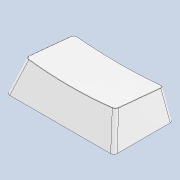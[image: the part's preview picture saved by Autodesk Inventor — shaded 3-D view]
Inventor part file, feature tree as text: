
AUTODESK INVENTOR PART (.ipt)
format: ipt  version: 2021 (Build 250183000, 183)  size: 241,664 bytes
history: native  units: in
note: dims shown in document units (in); Inventor stores cm internally (conversion verified against a paired STEP export)
features: chamfer x1
ambient origin geometry x8: Origin, YZ Plane, XZ Plane, XY Plane, X Axis, Y Axis, Z Axis, Center Point
bodies: Solid1 (feature_tree)
feature tree (1):
  chamfer  "Chamfer1"  [1 undecoded]
note: 1 required parameter value undecoded (feature->parameter linkage not recoverable at this tier; creation-order binding heuristic only, values carry confidence <= 0.55)
